# Revit family: Bernhardt_Design-Tables-Freestanding-Frame-Block_30h-Blueprint
name_source: partatom
category: Furniture
revit_build: Autodesk Revit 2016 (Build: 20150714_1515(x64)
units: mm (PartAtom-declared; Revit-internal decimal feet)

## family parameters
Always vertical = Yes
Cut with Voids When Loaded = No
OmniClass Number = 23.40.20.00
OmniClass Title = General Furniture and Specialties
Room Calculation Point = No
Shared = No
Work Plane-Based = No

## types (9) — shared parameters
BlackPaint = Black Paint
Blueprint Gray = Blueprint Gray
LegHeight = 28 3/4"
Manufacturer = Bernhardt Design
Model = Blueprint
RailCap = 0"
RailCapFront = 2"
TableTop = <By Category>
TableTopHeight = 28 3/4"
TotalHeight = 30"
URL = http://www.bernhardtdesign.com
Wood = <By Category>

## per-type parameters (varying)
| type | CapDistance_left | CapDistance_right | LegDistance | Railing_bottom | Railing_top | TableDepth | TableWidth_left | TableWidth_right | TotalDepth | TotalWidth |
| BPS-AGC-AC | 23 1/4" | 23 1/4" | 20" | -12 3/4" | 12 3/4" | 24" | 44 3/4" | 27 1/4" | 48" | 72" |
| BPS-AKC-AC | 35 1/4" | 35 1/4" | 16" | -24 1/2" | 24 1/2" | 24" | 56 3/4" | 39 1/4" | 48" | 96" |
| BPS-AOC-AC | 47 1/4" | 47 1/4" | 16" | -38 9/16" | 38 9/16" | 24" | 68 3/4" | 51 1/4" | 48" | 120" |
| BPS-AGA-AC | 23 1/4" | 23 1/4" | 16" | -12 3/4" | 12 3/4" | 18" | 44 3/4" | 27 1/4" | 36" | 72" |
| BPS-AKA-AC | 35 1/4" | 35 1/4" | 16" | -24 1/2" | 24 1/2" | 18" | 56 3/4" | 39 1/4" | 36" | 96" |
| BPS-AOA-AC | 47 1/4" | 47 1/4" | 16" | -38 9/16" | 38 9/16" | 18" | 68 3/4" | 51 1/4" | 36" | 120" |
| BPS-AGB-AC | 23 1/4" | 23 1/4" | 16" | -12 3/4" | 12 3/4" | 21" | 44 3/4" | 27 1/4" | 42" | 72" |
| BPS-AKB-AC | 35 1/4" | 35 1/4" | 16" | -24 1/2" | 24 1/2" | 21" | 56 3/4" | 39 1/4" | 42" | 96" |
| BPS-AOB-AC | 47 1/4" | 47 1/4" | 16" | -38 9/16" | 38 9/16" | 21" | 68 3/4" | 51 1/4" | 42" | 120" |

note: column(s) folded — value = type name in every type: Catalog, SKU

## geometry (parser evidence)
native form markers: Blend x2, Sweep x4
no freeform markers — native parametric forms only
